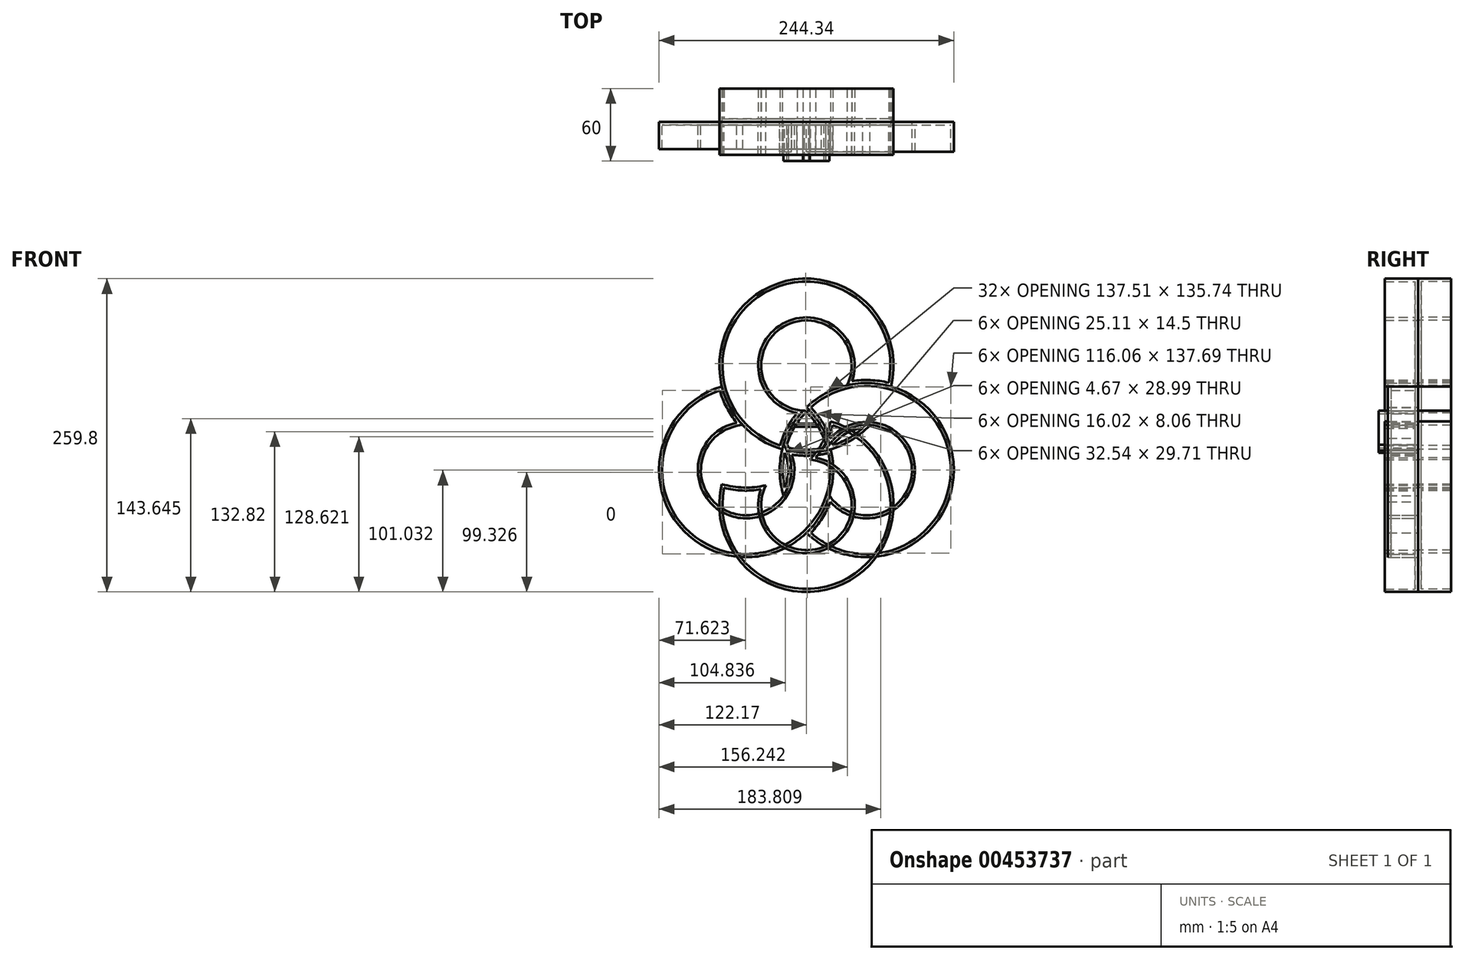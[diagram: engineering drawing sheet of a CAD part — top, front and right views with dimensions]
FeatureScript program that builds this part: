
annotation { "Feature Type Name" : "Feature", "Feature Type Description" : "" }
export const myFeature = defineFeature(function(context is Context, id is Id, definition is map)
    precondition{}
    {
        {
            var Q0;
            Q0=qCreatedBy(makeId("Front.planeOp"),FACE);
            var sketch = newSketch(context, id + "F0", { "sketchPlane" : qUnion([Q0])});
            skCircle(sketch, "E0.cCircle", {"center": v(0, 0) * mm, "radius": 7.22 * mm, "construction": true});
            skLineSegment(sketch, "E0.0", {"start": v(12.5, 7.22) * mm, "end": v(0, -14.43) * mm});
            skLineSegment(sketch, "E0.1", {"start": v(0, -14.43) * mm, "end": v(-12.5, 7.22) * mm});
            skLineSegment(sketch, "E0.2", {"start": v(-12.5, 7.22) * mm, "end": v(12.5, 7.22) * mm});
            skPoint(sketch, "E0.0.midPoint", {"position": v(6.25, -3.6) * mm});
            skCircle(sketch, "E1.cCircle", {"center": v(0, 0) * mm, "radius": 57.74 * mm, "construction": true});
            skLineSegment(sketch, "E1.0", {"start": v(50, -28.87) * mm, "end": v(-50, -28.87) * mm, "construction": true});
            skLineSegment(sketch, "E1.1", {"start": v(-50, -28.87) * mm, "end": v(0, 57.74) * mm, "construction": true});
            skLineSegment(sketch, "E1.2", {"start": v(0, 57.74) * mm, "end": v(50, -28.87) * mm, "construction": true});
            skArc(sketch, "E2", {"start": v(-70.07, 40.45) * mm, "mid": v(-48.01, -101) * mm, "end": v(-33.78, 41.46) * mm});
            skArc(sketch, "E3", {"start": v(0, -80.9) * mm, "mid": v(111.48, 8.93) * mm, "end": v(-19.01, -49.98) * mm});
            skArc(sketch, "E4", {"start": v(70.07, 40.45) * mm, "mid": v(-63.47, 92.08) * mm, "end": v(52.8, 8.53) * mm});
            skArc(sketch, "E5", {"start": v(-52.8, 8.53) * mm, "mid": v(-66.28, -62.65) * mm, "end": v(-19.01, -7.75) * mm});
            skArc(sketch, "E6", {"start": v(19.01, -49.98) * mm, "mid": v(87.4, -26.08) * mm, "end": v(16.22, -12.59) * mm});
            skArc(sketch, "E7", {"start": v(33.78, 41.46) * mm, "mid": v(-21.12, 88.72) * mm, "end": v(2.8, 20.34) * mm});
            skSolve(sketch);
        }
        {
            var Q0;
            Q0=qCreatedBy(makeId("Right.planeOp"),FACE);
            var sketch = newSketch(context, id + "F1", { "sketchPlane" : qUnion([Q0])});
            skLineSegment(sketch, "E8", {"start": v(0, 0) * mm, "end": v(-138.06, 0) * mm});
            skSolve(sketch);
        }
        {
            var Q0;
            {var subQ0=sQuery(id+"F0.wireOp",EDGE,"E2");var subQ9=sQuery(id+"F0.wireOp",EDGE,"E3");var subQ11=makeQuery(id+"F0.imprint","INTERSECT",VERTEX,{"disambiguationData":[OD(0.0)],"derivedFrom":[subQ0,subQ9]});Q0=makeQuery(id+"F0.imprint","IMPRINT",FACE,{"disambiguationData":[TD([[makeQuery(id+"F0.imprint","IMPRINT",EDGE,{"disambiguationData":[TD([[subQ11,-1.0]])],"derivedFrom":subQ0}),-1.0]])]});}
            var Q1;
            {var subQ0=sQuery(id+"F0.wireOp",EDGE,"E5");var subQ1=sQuery(id+"F0.wireOp",EDGE,"E3");var subQ2=makeQuery(id+"F0.imprint","INTERSECT",VERTEX,{"disambiguationData":[OD(0.0)],"derivedFrom":[subQ1,subQ0]});Q1=makeQuery(id+"F0.imprint","IMPRINT",FACE,{"disambiguationData":[TD([[makeQuery(id+"F0.imprint","IMPRINT",EDGE,{"disambiguationData":[TD([[subQ2,1.0]])],"derivedFrom":subQ1}),1.0]])]});}
            var Q2;
            {var subQ0=sQuery(id+"F0.wireOp",EDGE,"E5");var subQ1=sQuery(id+"F0.wireOp",EDGE,"E3");var subQ2=makeQuery(id+"F0.imprint","INTERSECT",VERTEX,{"disambiguationData":[OD(1.0)],"derivedFrom":[subQ1,subQ0]});Q2=makeQuery(id+"F0.imprint","IMPRINT",FACE,{"disambiguationData":[TD([[makeQuery(id+"F0.imprint","IMPRINT",EDGE,{"disambiguationData":[TD([[subQ2,-1.0]])],"derivedFrom":subQ1}),1.0]])]});}
            extrude(context, id + "F2", {"entities" : qUnion([Q0, Q1, Q2]), "depth" : 25 * mm});
        }
        {
            var Q0;
            {var subQ0=sQuery(id+"F0.wireOp",EDGE,"E3");var subQ6=sQuery(id+"F0.wireOp",EDGE,"E4");var subQ8=makeQuery(id+"F0.imprint","INTERSECT",VERTEX,{"disambiguationData":[OD(0.0)],"derivedFrom":[subQ0,subQ6]});Q0=makeQuery(id+"F0.imprint","IMPRINT",FACE,{"disambiguationData":[TD([[makeQuery(id+"F0.imprint","IMPRINT",EDGE,{"disambiguationData":[TD([[subQ8,-1.0]])],"derivedFrom":subQ0}),-1.0]])]});}
            var Q1;
            {var subQ0=sQuery(id+"F0.wireOp",EDGE,"E4");var subQ1=sQuery(id+"F0.wireOp",EDGE,"E2");var subQ2=makeQuery(id+"F0.imprint","INTERSECT",VERTEX,{"disambiguationData":[OD(1.0)],"derivedFrom":[subQ1,subQ0]});Q1=makeQuery(id+"F0.imprint","IMPRINT",FACE,{"disambiguationData":[TD([[makeQuery(id+"F0.imprint","IMPRINT",EDGE,{"disambiguationData":[TD([[subQ2,-1.0]])],"derivedFrom":subQ1}),-1.0]])]});}
            var Q2;
            {var subQ0=sQuery(id+"F0.wireOp",EDGE,"E4");var subQ1=sQuery(id+"F0.wireOp",EDGE,"E2");var subQ2=makeQuery(id+"F0.imprint","INTERSECT",VERTEX,{"disambiguationData":[OD(1.0)],"derivedFrom":[subQ1,subQ0]});Q2=makeQuery(id+"F0.imprint","IMPRINT",FACE,{"disambiguationData":[TD([[makeQuery(id+"F0.imprint","IMPRINT",EDGE,{"disambiguationData":[TD([[subQ2,-1.0]])],"derivedFrom":subQ1}),1.0]])]});}
            extrude(context, id + "F3", {"entities" : qUnion([Q0, Q1, Q2]), "depth" : 27.5 * mm});
        }
        {
            var Q0;
            {var subQ0=sQuery(id+"F0.wireOp",EDGE,"E4");var subQ1=sQuery(id+"F0.wireOp",EDGE,"E2");var subQ2=makeQuery(id+"F0.imprint","INTERSECT",VERTEX,{"disambiguationData":[OD(0.0)],"derivedFrom":[subQ1,subQ0]});Q0=makeQuery(id+"F0.imprint","IMPRINT",FACE,{"disambiguationData":[TD([[makeQuery(id+"F0.imprint","IMPRINT",EDGE,{"disambiguationData":[TD([[subQ2,-1.0]])],"derivedFrom":subQ1}),1.0]])]});}
            var Q1;
            {var subQ0=sQuery(id+"F0.wireOp",EDGE,"E7");var subQ1=sQuery(id+"F0.wireOp",EDGE,"E2");var subQ2=makeQuery(id+"F0.imprint","INTERSECT",VERTEX,{"disambiguationData":[OD(0.0)],"derivedFrom":[subQ1,subQ0]});Q1=makeQuery(id+"F0.imprint","IMPRINT",FACE,{"disambiguationData":[TD([[makeQuery(id+"F0.imprint","IMPRINT",EDGE,{"disambiguationData":[TD([[subQ2,1.0]])],"derivedFrom":subQ1}),1.0]])]});}
            var Q2;
            {var subQ0=sQuery(id+"F0.wireOp",EDGE,"E7");var subQ1=sQuery(id+"F0.wireOp",EDGE,"E2");var subQ2=makeQuery(id+"F0.imprint","INTERSECT",VERTEX,{"disambiguationData":[OD(1.0)],"derivedFrom":[subQ1,subQ0]});Q2=makeQuery(id+"F0.imprint","IMPRINT",FACE,{"disambiguationData":[TD([[makeQuery(id+"F0.imprint","IMPRINT",EDGE,{"disambiguationData":[TD([[subQ2,-1.0]])],"derivedFrom":subQ1}),1.0]])]});}
            extrude(context, id + "F4", {"entities" : qUnion([Q0, Q1, Q2]), "depth" : 22.5 * mm});
        }
        {
            var Q0;
            Q0=makeQuery(id+"F0.imprint","IMPRINT",FACE,{"disambiguationData":[TD([[makeQuery(id+"F0.imprint","IMPRINT",EDGE,{"derivedFrom":sQuery(id+"F0.wireOp",EDGE,"E0.0")}),-1.0]])]});
            var Q1;
            {var subQ0=sQuery(id+"F0.wireOp",EDGE,"E0.2");Q1=makeQuery(id+"F0.imprint","IMPRINT",FACE,{"disambiguationData":[TD([[makeQuery(id+"F0.imprint","IMPRINT",EDGE,{"derivedFrom":subQ0}),1.0]])]});}
            var Q2;
            {var subQ0=sQuery(id+"F0.wireOp",EDGE,"E0.1");Q2=makeQuery(id+"F0.imprint","IMPRINT",FACE,{"disambiguationData":[TD([[makeQuery(id+"F0.imprint","IMPRINT",EDGE,{"derivedFrom":subQ0}),1.0]])]});}
            var Q3;
            {var subQ0=sQuery(id+"F0.wireOp",EDGE,"E0.0");Q3=makeQuery(id+"F0.imprint","IMPRINT",FACE,{"disambiguationData":[TD([[makeQuery(id+"F0.imprint","IMPRINT",EDGE,{"derivedFrom":subQ0}),1.0]])]});}
            extrude(context, id + "F5", {"entities" : qUnion([Q0, Q1, Q2, Q3]), "depth" : 32.5 * mm});
        }
        {
            var Q0;
            Q0=makeQuery(id+"F3.opExtrude","CAP_FACE",FACE,{"disambiguationData":[OSD([sQuery(id+"F0.wireOp",EDGE,"E3"),sQuery(id+"F0.wireOp",EDGE,"E4"),sQuery(id+"F0.wireOp",EDGE,"E7")])],"isStart":false});
            var Q1;
            Q1=makeQuery(id+"F2.opExtrude","CAP_FACE",FACE,{"disambiguationData":[OSD([sQuery(id+"F0.wireOp",EDGE,"E2"),sQuery(id+"F0.wireOp",EDGE,"E3"),sQuery(id+"F0.wireOp",EDGE,"E6")])],"isStart":false});
            var Q2;
            Q2=makeQuery(id+"F4.opExtrude","CAP_FACE",FACE,{"disambiguationData":[OSD([sQuery(id+"F0.wireOp",EDGE,"E2"),sQuery(id+"F0.wireOp",EDGE,"E4"),sQuery(id+"F0.wireOp",EDGE,"E5")])],"isStart":false});
            var Q3;
            Q3=makeQuery(id+"F4.opExtrude","CAP_FACE",FACE,{"disambiguationData":[OSD([sQuery(id+"F0.wireOp",EDGE,"E2"),sQuery(id+"F0.wireOp",EDGE,"E7")])],"isStart":false});
            var Q4;
            Q4=makeQuery(id+"F2.opExtrude","CAP_FACE",FACE,{"disambiguationData":[OSD([sQuery(id+"F0.wireOp",EDGE,"E3"),sQuery(id+"F0.wireOp",EDGE,"E5")])],"isStart":false});
            var Q5;
            Q5=makeQuery(id+"F3.opExtrude","CAP_FACE",FACE,{"disambiguationData":[OSD([sQuery(id+"F0.wireOp",EDGE,"E4"),sQuery(id+"F0.wireOp",EDGE,"E6")])],"isStart":false});
            var Q6;
            Q6=makeQuery(id+"F5.opExtrude","CAP_FACE",FACE,{"disambiguationData":[OSD([sQuery(id+"F0.wireOp",EDGE,"E2"),sQuery(id+"F0.wireOp",EDGE,"E3"),sQuery(id+"F0.wireOp",EDGE,"E4"),sQuery(id+"F0.wireOp",EDGE,"E5"),sQuery(id+"F0.wireOp",EDGE,"E6"),sQuery(id+"F0.wireOp",EDGE,"E7")])],"isStart":false});
            shell(context, id + "F6", {"entities" : qUnion([Q0, Q1, Q2, Q3, Q4, Q5, Q6]), "thickness" : 2.5 * mm});
        }
        {
            var Q0;
            Q0=makeQuery(id+"F3.opExtrude","SWEPT_BODY",BODY,{"disambiguationData":[OSD([sQuery(id+"F0.wireOp",EDGE,"E3"),sQuery(id+"F0.wireOp",EDGE,"E4"),sQuery(id+"F0.wireOp",EDGE,"E7")])]});
            var Q1;
            Q1=qCreatedBy(makeId("Front.planeOp"),FACE);
            mirror(context, id + "F7", {"entities" : qUnion([Q0]), "mirrorPlane" : qUnion([Q1])});
        }
        {
            var Q0;
            Q0=makeQuery(id+"F7.opPattern","COPY",BODY,{"derivedFrom":makeQuery(id+"F3.opExtrude","SWEPT_BODY",BODY,{"disambiguationData":[OSD([sQuery(id+"F0.wireOp",EDGE,"E3"),sQuery(id+"F0.wireOp",EDGE,"E4"),sQuery(id+"F0.wireOp",EDGE,"E7")])]}),"instanceName":"1"});
            var Q1;
            Q1=makeQuery(id+"F3.opExtrude","SWEPT_BODY",BODY,{"disambiguationData":[OSD([sQuery(id+"F0.wireOp",EDGE,"E3"),sQuery(id+"F0.wireOp",EDGE,"E4"),sQuery(id+"F0.wireOp",EDGE,"E7")])]});
            var Q2;
            Q2=sQuery(id+"F1.wireOp",EDGE,"E8");
            circularPattern(context, id + "F8", {"entities" : qUnion([Q0, Q1]), "axis" : qUnion([Q2]), "angle" : 180 * degree, "instanceCount" : 2, "equalSpace" : true});
        }
    });
